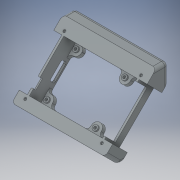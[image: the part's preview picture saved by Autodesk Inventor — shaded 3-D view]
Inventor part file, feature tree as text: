
AUTODESK INVENTOR PART (.ipt)
format: ipt  version: 2019 (Build 230136000, 136)  size: 337,408 bytes
history: native  units: in
note: dims shown in document units (in); Inventor stores cm internally (conversion verified against a paired STEP export)
features: extrude x2, sketch x2, other x1, fillet x1, projected_geometry x1, imported_body x1
ambient origin geometry x8: Origin, YZ Plane, XZ Plane, XY Plane, X Axis, Y Axis, Z Axis, Center Point
bodies: Body1 (feature_tree)
feature tree (8):
  other  "實體1"
  extrude  "擠出1"  TaperAngle=0.0deg  [1 undecoded]
  fillet  "圓角1"  Radius=0.1575in
  extrude  "擠出2"  Depth=0.2756in
  sketch  "草圖1"
  sketch  "草圖2"
  projected_geometry  "投影迴路1"
  imported_body  "Base1"
note: 1 required parameter value undecoded (feature->parameter linkage not recoverable at this tier; creation-order binding heuristic only, values carry confidence <= 0.55)
